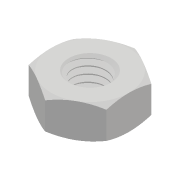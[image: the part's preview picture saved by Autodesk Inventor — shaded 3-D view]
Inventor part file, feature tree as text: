
AUTODESK INVENTOR PART (.ipt)
format: ipt  version: 2018 (Build 220112000, 112)  size: 318,976 bytes
history: native  units: mm
features: mirror x1
ambient origin geometry x8: Origin, YZ Plane, XZ Plane, XY Plane, X Axis, Y Axis, Z Axis, Center Point
bodies: Solid1 (feature_tree)
feature tree (1):
  mirror  "Mirror2"
